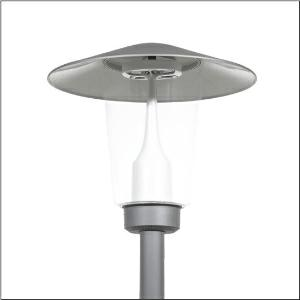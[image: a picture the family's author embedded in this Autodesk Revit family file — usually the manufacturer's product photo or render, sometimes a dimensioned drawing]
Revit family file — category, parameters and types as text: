
# Revit family: pilzleuchte_iq___st1_2a_5xa5235mf14hp_ceaa
name_source: partatom
category: Lighting Fixtures
units: mm (PartAtom-declared; Revit-internal decimal feet)

## family parameters
Cut with Voids When Loaded = No
Host = Face
Light Source = No
Part Type = Normal
Room Calculation Point = No
Round Connector Dimension = Use Diameter
Shared = No

## types (1)
- --- (1 x LED, 4280 lm, 33.6 W, 2700K)
    Apparent Load = 34 VA
    CIE Flux Codes = 23 60 92 98 100
    Color Rendering = 70
    Color Temperature = 2700K
    Default Elevation = 1800 mm
    Description = Mushroom Luminaire iQ, mast luminaire, Module 540 iQ-SR, primary light control with 3 zone facetted reflector, of plastic, silver coated, highly specular, structured, primary optical cover: cover, of PMMA, transparent, light distribution: ST1.2a, light emission: direct distribution, primary light characteristic: asymmetric, installation type: post-top, LED, High Power LED, rated luminous flux: 4.280lm, luminous efficacy: 127lm/W, light colour: 727, colour temperature: 2700K, control gear: ECG iQ, control: presetting dimming logarithmic, Street-Remote, Auto-Match, Temp-Guard, Lumen-Switch, Night-Set, Smart-Wire, Light-Fading, Desk-Remote (wireless, voltage-free reading and setting of iQ features in the workshop via application-optimized NFC function/RFID function), optimised constant luminous flux control (CLO 2.0), with terminal, 6-pole, max. 2.5mm², mains connection: 230..240V, AC, 50/60Hz, start of lifetime: 34W, end of service life: 36W, reduction: 15W, luminaire housing, upper part, of glass-fibre reinforced polyester, coated, Siteco® metallic grey (DB 702S), diameter: 650mm, height: 586mm, spigot size: d x l = 76 x 70mm (post-top) | with reducer (optional accessory) 60 x 70mm, post-top mast mounting element, of diecast aluminium, coated, Siteco® metallic grey (DB 702S), Module 540 iQ-SR, traffic white (RAL 9016), equipment: Power, protection rating (complete): IP65, insulation class (complete): insulation class II (safety insulation), certification: CE, ENEC, VDE, packaging unit: 1 piece

Light Distribution: ST1.2a
    Height = 586 mm
    Lamp = 1 x LED
    Lamp Light Flux = 4280 lm
    Lamp Power = 33.6 W
    Lamp count = 1
    Length = 650 mm
    Luminous efficacy = 127 lm/W
    Manufacturer = Siteco
    ModVariant = No
    Model = 5XA5235MF14HP
    Number of Poles = 1
    OnlyDefault = Yes
    Power Factor = 1
    Product Name = Pilzleuchte iQ | ST1.2a
    Product group = mast luminaire | pylon top
    ProductGroupID = 6100
    Protection Class = Protection class II
    Protection Degree = IP 65
    RLX_Detail_Level = 1
    RLX_Emergency_Light_Flux = 0 lm
    RLX_Emergency_Type = 0
    RLX_Emergency_Type_DB = No
    RlxData = <blob elided: 51729 chars, md5=8086b1a0>
    Socket = socket
    Standby Power = 0 W
    System Light Flux = 4280 lm
    System Power = 34 W
    Type Comments = factory setting: luminous flux: 100 % | dim-lin: 254 | 695 mA
    Type Image = l_1006077.jpg
    URL = http://relux.com
    VarID = @adj_102925
    Voltage = 0 V
    Weight = 0.00 kg
    Width = 0 mm  [stored 0 ft]

note: [stored X ft] marks values corroborated as IEEE doubles in the binary element streams (Revit-internal decimal feet)

## geometry (parser evidence)
native form markers: Blend x4, Sweep x12
no freeform markers — native parametric forms only
